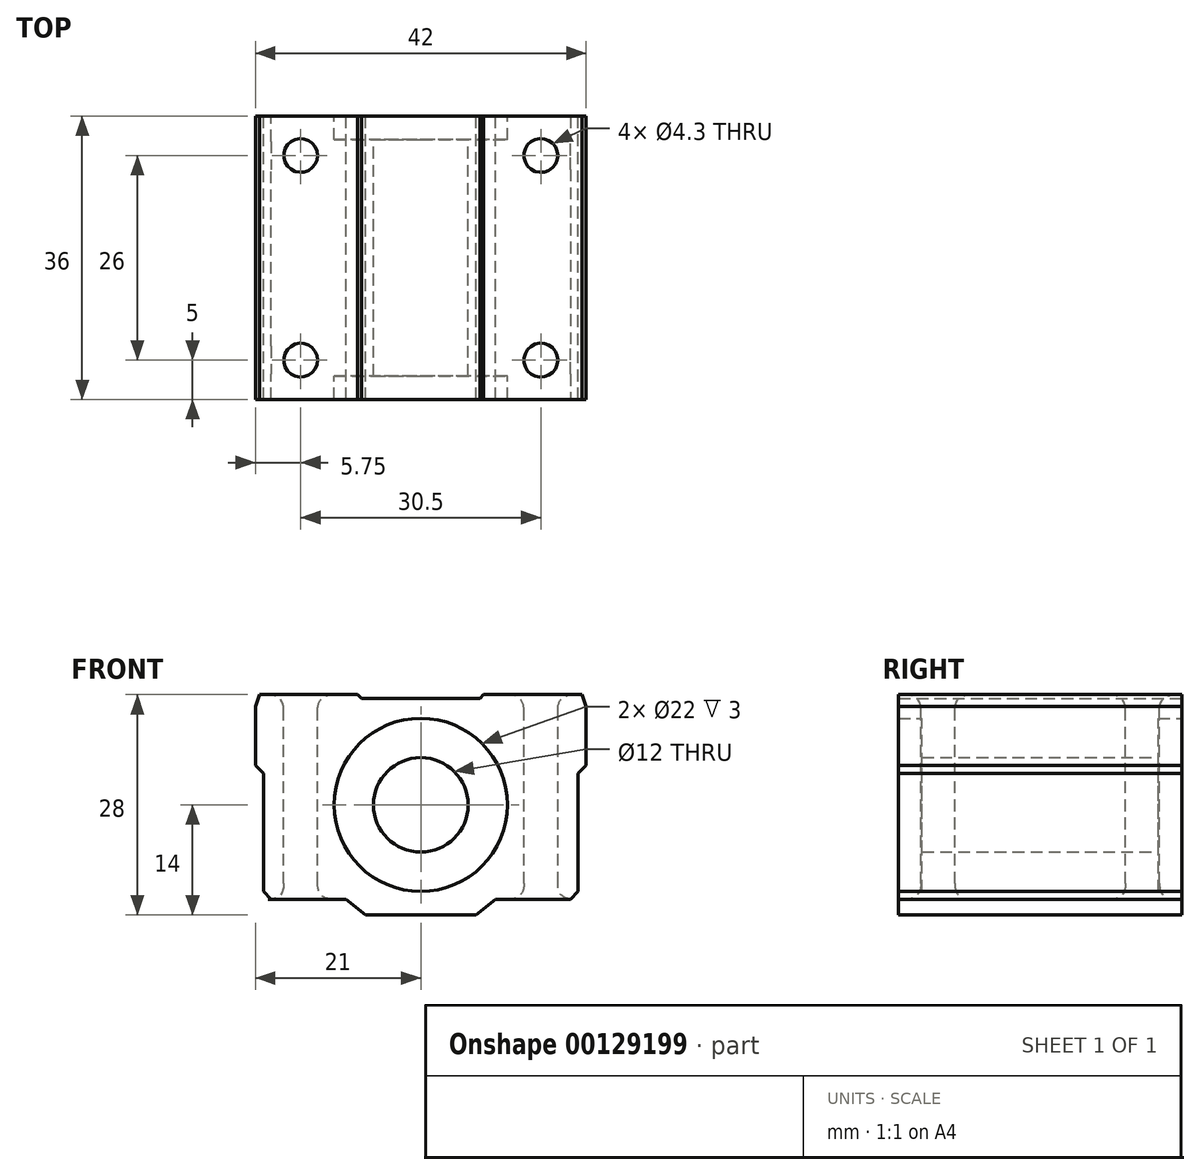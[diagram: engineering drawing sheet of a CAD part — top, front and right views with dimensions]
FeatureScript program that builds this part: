
annotation { "Feature Type Name" : "Feature", "Feature Type Description" : "" }
export const myFeature = defineFeature(function(context is Context, id is Id, definition is map)
    precondition{}
    {
        {
            var Q0;
            Q0=qCreatedBy(makeId("Front.planeOp"),FACE);
            var sketch = newSketch(context, id + "F0", { "sketchPlane" : qUnion([Q0])});
            skLineSegment(sketch, "E0.bottom", {"start": v(-20.5, 14) * mm, "end": v(-8, 14) * mm});
            skLineSegment(sketch, "E0.top", {"start": v(-7, -14) * mm, "end": v(7, -14) * mm});
            skLineSegment(sketch, "E0.left", {"start": v(-21, 12.5) * mm, "end": v(-21, 5) * mm});
            skLineSegment(sketch, "E0.right", {"start": v(21, 12.5) * mm, "end": v(21, 5) * mm});
            skLineSegment(sketch, "E1", {"start": v(-20, -12) * mm, "end": v(-9.5, -12) * mm});
            skCircle(sketch, "E2", {"center": v(0, 0) * mm, "radius": 6 * mm});
            skCircle(sketch, "E3", {"center": v(0, 0) * mm, "radius": 11 * mm});
            skLineSegment(sketch, "E4", {"start": v(20, 4) * mm, "end": v(20, -12) * mm});
            skLineSegment(sketch, "E5", {"start": v(7, -14) * mm, "end": v(9.5, -12) * mm});
            skLineSegment(sketch, "E6", {"start": v(-7, -14) * mm, "end": v(-9.5, -12) * mm});
            skLineSegment(sketch, "E7", {"start": v(-21, 5) * mm, "end": v(-20, 4) * mm});
            skLineSegment(sketch, "E8", {"start": v(21, 5) * mm, "end": v(20, 4) * mm});
            skLineSegment(sketch, "E9", {"start": v(21, 12.5) * mm, "end": v(20.5, 14) * mm});
            skLineSegment(sketch, "E10", {"start": v(8, 14) * mm, "end": v(7.5, 13.5) * mm});
            skLineSegment(sketch, "E11", {"start": v(-8, 14) * mm, "end": v(-7.5, 13.5) * mm});
            skLineSegment(sketch, "E12", {"start": v(-21, 12.5) * mm, "end": v(-20.5, 14) * mm});
            skLineSegment(sketch, "E13.trimOffspring", {"start": v(-20, 4) * mm, "end": v(-20, -12) * mm});
            skLineSegment(sketch, "E14.trimOffspring", {"start": v(8, 14) * mm, "end": v(20.5, 14) * mm});
            skLineSegment(sketch, "E15.trimOffspring", {"start": v(-7.5, 13.5) * mm, "end": v(7.5, 13.5) * mm});
            skLineSegment(sketch, "E16.trimOffspring", {"start": v(9.5, -12) * mm, "end": v(20, -12) * mm});
            skCircle(sketch, "E17", {"center": v(0, 0) * mm, "radius": 12 * mm});
            skSolve(sketch);
        }
        {
            var Q0;
            Q0=makeQuery(id+"F0.imprint","IMPRINT",FACE,{"disambiguationData":[TD([[makeQuery(id+"F0.imprint","IMPRINT",EDGE,{"derivedFrom":sQuery(id+"F0.wireOp",EDGE,"E0.top")}),1.0]])]});
            var Q1;
            Q1=makeQuery(id+"F0.imprint","IMPRINT",FACE,{"disambiguationData":[TD([[makeQuery(id+"F0.imprint","IMPRINT",EDGE,{"derivedFrom":sQuery(id+"F0.wireOp",EDGE,"E3")}),-1.0]])]});
            extrude(context, id + "F1", {"entities" : qUnion([Q0, Q1]), "endBound" : BoundingType.SYMMETRIC, "depth" : 36 * mm});
        }
        {
            var Q0;
            Q0=makeQuery(id+"F1.opExtrude","SWEPT_EDGE",EDGE,{"disambiguationData":[OSD([sQuery(id+"F0.wireOp",EDGE,"E4"),sQuery(id+"F0.wireOp",EDGE,"E16.trimOffspring")])]});
            var Q1;
            Q1=makeQuery(id+"F1.opExtrude","SWEPT_EDGE",EDGE,{"disambiguationData":[OSD([sQuery(id+"F0.wireOp",EDGE,"E1"),sQuery(id+"F0.wireOp",EDGE,"E13.trimOffspring")])]});
            chamfer(context, id + "F2", {"entities" : qUnion([Q0, Q1]), "width" : 1 * mm, "tangentPropagation" : true});
        }
        {
            var Q0;
            Q0=qCreatedBy(makeId("Front.planeOp"),FACE);
            cPlane(context, id + "F3", {"entities" : qUnion([Q0]), "cplaneType" : CPlaneType.OFFSET, "offset" : 14.5 * mm, "width" : 150 * mm, "height" : 150 * mm});
        }
        {
            var Q0;
            Q0=makeQuery(id+"F0.imprint","IMPRINT",FACE,{"disambiguationData":[TD([[makeQuery(id+"F0.imprint","IMPRINT",EDGE,{"derivedFrom":sQuery(id+"F0.wireOp",EDGE,"E2")}),-1.0]])]});
            var Q1;
            Q1=makeQuery(id+"F0.imprint","IMPRINT",FACE,{"disambiguationData":[TD([[makeQuery(id+"F0.imprint","IMPRINT",EDGE,{"derivedFrom":sQuery(id+"F0.wireOp",EDGE,"E3")}),-1.0]])]});
            extrude(context, id + "F4", {"entities" : qUnion([Q0, Q1]), "operationType" : NewBodyOperationType.ADD, "endBound" : BoundingType.SYMMETRIC, "depth" : 30 * mm});
        }
        {
            var Q0;
            Q0=qCreatedBy(makeId("Top.planeOp"),FACE);
            var sketch = newSketch(context, id + "F5", { "sketchPlane" : qUnion([Q0])});
            skLineSegment(sketch, "E18", {"start": v(-15.25, 31.05) * mm, "end": v(-15.25, -40.2) * mm, "construction": true});
            skLineSegment(sketch, "E19", {"start": v(15.25, 27.94) * mm, "end": v(15.25, -41.57) * mm, "construction": true});
            skLineSegment(sketch, "E20", {"start": v(-34.75, -13) * mm, "end": v(38.45, -13) * mm, "construction": true});
            skLineSegment(sketch, "E21", {"start": v(38.45, 13) * mm, "end": v(-33.97, 13) * mm, "construction": true});
            skCircle(sketch, "E22", {"center": v(-15.25, 13) * mm, "radius": 2.15 * mm});
            skCircle(sketch, "E23", {"center": v(15.25, 13) * mm, "radius": 2.15 * mm});
            skCircle(sketch, "E24", {"center": v(15.25, -13) * mm, "radius": 2.15 * mm});
            skCircle(sketch, "E25", {"center": v(-15.25, -13) * mm, "radius": 2.15 * mm});
            skSolve(sketch);
        }
        {
            var Q0;
            Q0=makeQuery(id+"F5.imprint","IMPRINT",FACE,{"disambiguationData":[TD([[makeQuery(id+"F5.imprint","IMPRINT",EDGE,{"derivedFrom":sQuery(id+"F5.wireOp",EDGE,"E22")}),1.0]])]});
            var Q1;
            Q1=makeQuery(id+"F5.imprint","IMPRINT",FACE,{"disambiguationData":[TD([[makeQuery(id+"F5.imprint","IMPRINT",EDGE,{"derivedFrom":sQuery(id+"F5.wireOp",EDGE,"E25")}),1.0]])]});
            var Q2;
            Q2=makeQuery(id+"F5.imprint","IMPRINT",FACE,{"disambiguationData":[TD([[makeQuery(id+"F5.imprint","IMPRINT",EDGE,{"derivedFrom":sQuery(id+"F5.wireOp",EDGE,"E24")}),1.0]])]});
            var Q3;
            Q3=makeQuery(id+"F5.imprint","IMPRINT",FACE,{"disambiguationData":[TD([[makeQuery(id+"F5.imprint","IMPRINT",EDGE,{"derivedFrom":sQuery(id+"F5.wireOp",EDGE,"E23")}),1.0]])]});
            extrude(context, id + "F6", {"entities" : qUnion([Q0, Q1, Q2, Q3]), "operationType" : NewBodyOperationType.REMOVE, "endBound" : BoundingType.SYMMETRIC, "oppositeDirection" : true, "depth" : 30 * mm});
        }
        {
            var Q0;
            Q0=makeQuery(id+"F6.boolean.opBoolean","COPY",FACE,{"derivedFrom":makeQuery(id+"F6.opExtrude","SWEPT_FACE",FACE,{"disambiguationData":[OSD([sQuery(id+"F5.wireOp",EDGE,"E25")])]})});
            var Q1;
            Q1=makeQuery(id+"F6.boolean.opBoolean","COPY",FACE,{"derivedFrom":makeQuery(id+"F6.opExtrude","SWEPT_FACE",FACE,{"disambiguationData":[OSD([sQuery(id+"F5.wireOp",EDGE,"E24")])]})});
            var Q2;
            Q2=makeQuery(id+"F6.boolean.opBoolean","COPY",FACE,{"derivedFrom":makeQuery(id+"F6.opExtrude","SWEPT_FACE",FACE,{"disambiguationData":[OSD([sQuery(id+"F5.wireOp",EDGE,"E23")])]})});
            var Q3;
            Q3=makeQuery(id+"F6.boolean.opBoolean","COPY",FACE,{"derivedFrom":makeQuery(id+"F6.opExtrude","SWEPT_FACE",FACE,{"disambiguationData":[OSD([sQuery(id+"F5.wireOp",EDGE,"E22")])]})});
            fillet(context, id + "F7", {"entities" : qUnion([Q0, Q1, Q2, Q3]), "radius" : 2 * mm, "tangentPropagation" : true, "rho" : 0.5, "crossSection" : FilletCrossSection.CONIC, "allowEdgeOverflow" : false});
        }
    });
